# Revit family: NAU_Naughtone_Stng_Polly_Stools1
name_source: partatom
category: Furniture
revit_build: Autodesk Revit 2015 (Build: 20140903_1530(x64)
units: mm (PartAtom-declared; Revit-internal decimal feet)

## types (2) — shared parameters
AdditionalMaterials = Additional material and finish options available. Please contact Naughtone direct for further information.
Assembly Code = E2020200
AssetType = Movable
BIMObjectName = NAU_Naughtone_Seating_Polly_Stools
Category = Pr_40_50_12_85 Stools
Color = Various
ComponentDescription = The Polly chair fundamentally provides a very comfortable ergonomic seat with as little visual detail as possible. The Polypropylene seat shell has subtle edge details, a soft texture and just the right amount of flex, all of which combine to provide a tactile and satisfying sitting experience.
DurationUnit = year
Finish = Polypropylene
IfcExportAs = IfcFurnishingElementType
IfcExportType = STOOL
Keynote = Pr_40_50_12_85
MainColor = Various
ManufacturerAddressUK = Knaresborough Tech Park, Manse Lane, Knaresborough, HG5 8LF
ManufacturerName = Naughtone
ManufacturerURL = www.naughtone.com
Material = Steel/plastic
NBSDescription = Seating
NBSReference = 45-35-72/352
Name = Seating_Stools_Naughtone
NominalLength = 568 mm  [stored 1.86352 ft]
NominalWidth = 536 mm  [stored 1.75853 ft]
ProductInformation = www.naughtone.com/portfolio-view/polly
ReplacementCost = 0.00
Shape = Rectangular
SustainabilityPerformance = FSC certified. FISP certified. ISO 14001
URL = www.naughtone.com
Uniclass2015Description = Stools
Uniclass2015Reference = Pr_40_50_12_85
Uniclass2015Version = Products v1.6
Version = 1
WarrantyDescription = Request warranty information from naughtone
WarrantyDurationLabor = 5
WarrantyDurationParts = 5
WarrantyDurationUnit = year
zero-valued in all types: Cost

## per-type parameters (varying)
| type | Description | IsPOLLYBSB4L | IsPOLLYCHBSB4L | Model | ModelNumber | ModelReference | NominalHeight | SeatHeight | Size |
| POLLYBSB4L | Polly Bar Stool | Yes | No | POLYBSBS4L | POLYBSBS4L | Polly Bar Stool | 1105 mm  [stored 3.62533 ft] | 750 mm  [stored 2.46063 ft] | 568x536x1105mm |
| POLLYCHSB4L | Polly Counter Height Stool | No | Yes | POLLYCHSB4L | POLLYCHSB4L | Polly Counter Height Stool | 1005 mm  [stored 3.29724 ft] | 650 mm  [stored 2.13255 ft] | 568x536x1005mm |

note: [stored X ft] marks values corroborated as IEEE doubles in the binary element streams (Revit-internal decimal feet)

## geometry (parser evidence)
native form markers: Sweep x4
no freeform markers — native parametric forms only
